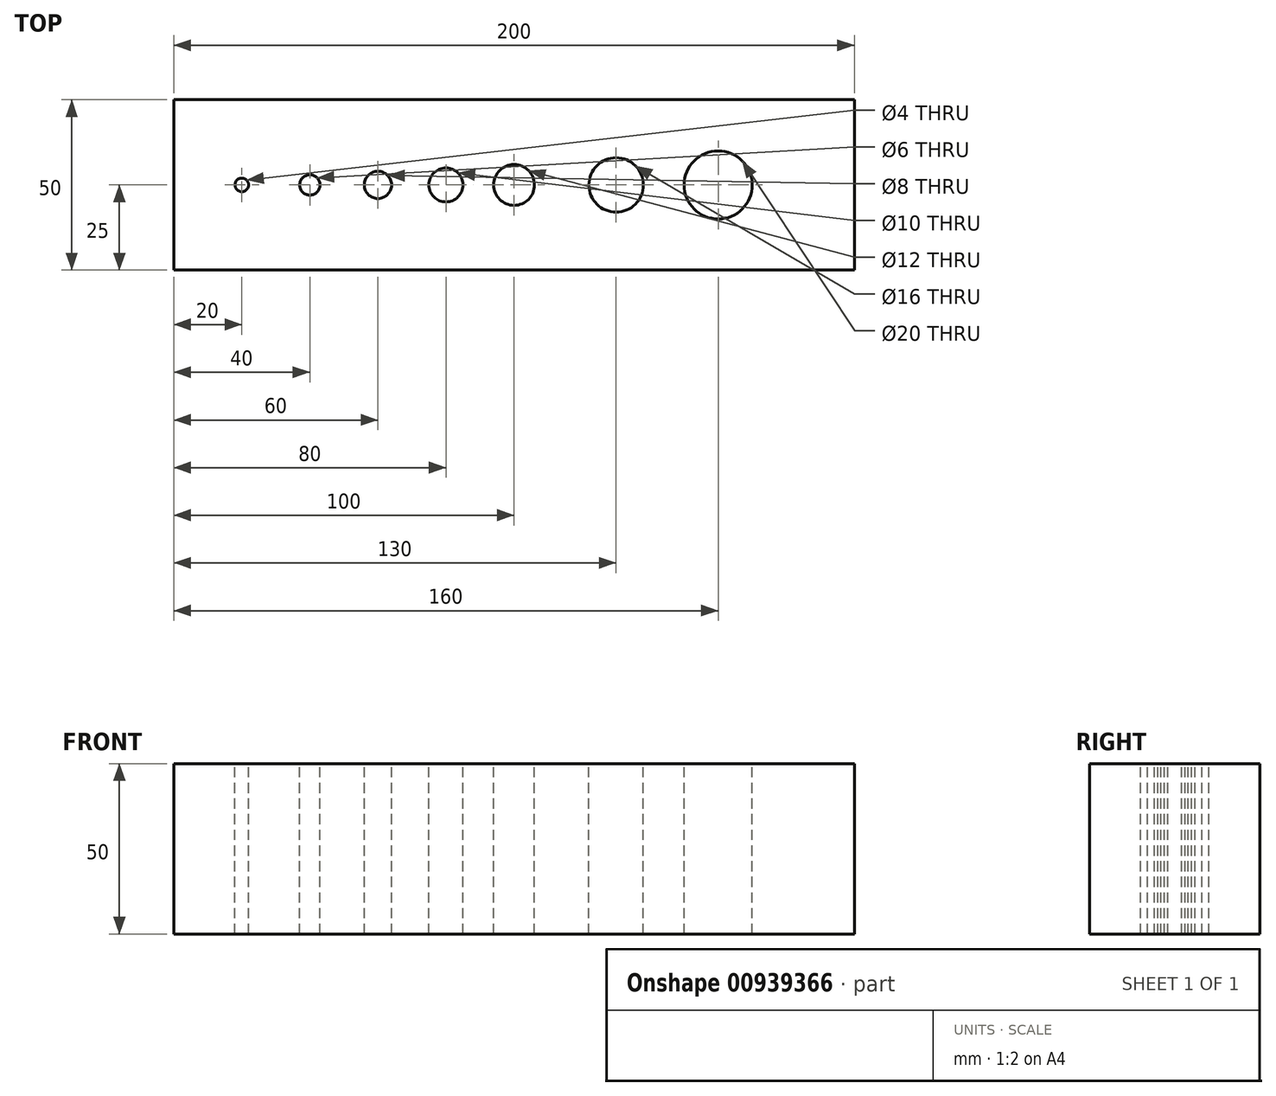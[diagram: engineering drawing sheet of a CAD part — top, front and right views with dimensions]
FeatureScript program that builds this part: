
annotation { "Feature Type Name" : "Feature", "Feature Type Description" : "" }
export const myFeature = defineFeature(function(context is Context, id is Id, definition is map)
    precondition{}
    {
        {
            var Q0;
            Q0=qCreatedBy(makeId("Top.planeOp"),FACE);
            var sketch = newSketch(context, id + "F0", { "sketchPlane" : qUnion([Q0])});
            skLineSegment(sketch, "E0.bottom", {"start": v(-100, 25) * mm, "end": v(100, 25) * mm});
            skLineSegment(sketch, "E0.top", {"start": v(-100, -25) * mm, "end": v(100, -25) * mm});
            skLineSegment(sketch, "E0.left", {"start": v(-100, 25) * mm, "end": v(-100, -25) * mm});
            skLineSegment(sketch, "E0.right", {"start": v(100, 25) * mm, "end": v(100, -25) * mm});
            skPoint(sketch, "E0.middle", {"position": v(0, 0) * mm});
            skSolve(sketch);
        }
        {
            var Q0;
            Q0=makeQuery(id+"F0.imprint","IMPRINT",FACE,{"disambiguationData":[TD([[makeQuery(id+"F0.imprint","IMPRINT",EDGE,{"derivedFrom":sQuery(id+"F0.wireOp",EDGE,"E0.bottom")}),-1.0]])]});
            extrude(context, id + "F1", {"entities" : qUnion([Q0]), "endBound" : BoundingType.SYMMETRIC, "depth" : 50 * mm, "offsetDistance" : 25.4 * mm});
        }
        {
            var Q0;
            Q0=makeQuery(id+"F1.opExtrude","CAP_FACE",FACE,{"disambiguationData":[OSD([sQuery(id+"F0.wireOp",EDGE,"E0.bottom"),sQuery(id+"F0.wireOp",EDGE,"E0.top"),sQuery(id+"F0.wireOp",EDGE,"E0.left"),sQuery(id+"F0.wireOp",EDGE,"E0.right")])],"isStart":false});
            var sketch = newSketch(context, id + "F2", { "sketchPlane" : qUnion([Q0])});
            skPoint(sketch, "E1", {"position": v(-80, 0) * mm});
            skPoint(sketch, "E2.1.0.0", {"position": v(-60, 0) * mm});
            skPoint(sketch, "E2.2.0.0", {"position": v(-40, 0) * mm});
            skPoint(sketch, "E2.3.0.0", {"position": v(-20, 0) * mm});
            skPoint(sketch, "E2.4.0.0", {"position": v(0, 0) * mm});
            skLineSegment(sketch, "E2.direction1", {"start": v(-80, 0) * mm, "end": v(-60, 0) * mm, "construction": true});
            skPoint(sketch, "E3.1.0.0", {"position": v(30, 0) * mm});
            skPoint(sketch, "E3.2.0.0", {"position": v(60, 0) * mm});
            skLineSegment(sketch, "E3.direction1", {"start": v(0, 0) * mm, "end": v(30, 0) * mm, "construction": true});
            skSolve(sketch);
        }
        {
            var Q0;
            Q0=sQuery(id+"F2.wireOp",VERTEX,"E2.direction1.start");
            var Q1;
            Q1=makeQuery(id+"F1.opExtrude","SWEPT_BODY",BODY,{"disambiguationData":[OSD([sQuery(id+"F0.wireOp",EDGE,"E0.bottom"),sQuery(id+"F0.wireOp",EDGE,"E0.top"),sQuery(id+"F0.wireOp",EDGE,"E0.left"),sQuery(id+"F0.wireOp",EDGE,"E0.right")])]});
            hole(context, id + "F3", {"style" : HoleStyle.SIMPLE, "endStyle" : HoleEndStyle.THROUGH, "standardTappedOrClearance" : lookupTablePath({ "standard" : "ISO", "size" : "4", "type" : "Drilled" }), "standardBlindInLast" : lookupTablePath({ "standard" : "ISO", "size" : "4", "type" : "Drilled" }), "holeDiameter" : 4 * mm, "majorDiameter" : 6.35 * mm, "tappedDepth" : 12.7 * mm, "tapClearance" : 3, "startFromSketch" : true, "locations" : qUnion([Q0]), "scope" : qUnion([Q1])});
        }
        {
            var Q0;
            Q0=sQuery(id+"F2.wireOp",VERTEX,"E2.direction1.end");
            var Q1;
            Q1=makeQuery(id+"F1.opExtrude","SWEPT_BODY",BODY,{"disambiguationData":[OSD([sQuery(id+"F0.wireOp",EDGE,"E0.bottom"),sQuery(id+"F0.wireOp",EDGE,"E0.top"),sQuery(id+"F0.wireOp",EDGE,"E0.left"),sQuery(id+"F0.wireOp",EDGE,"E0.right")])]});
            hole(context, id + "F4", {"style" : HoleStyle.SIMPLE, "endStyle" : HoleEndStyle.THROUGH, "standardTappedOrClearance" : lookupTablePath({ "standard" : "ISO", "size" : "6", "type" : "Drilled" }), "standardBlindInLast" : lookupTablePath({ "standard" : "ISO", "size" : "6", "type" : "Drilled" }), "holeDiameter" : 6 * mm, "majorDiameter" : 6.35 * mm, "tappedDepth" : 12.7 * mm, "tapClearance" : 3, "startFromSketch" : true, "locations" : qUnion([Q0]), "scope" : qUnion([Q1])});
        }
        {
            var Q0;
            Q0=sQuery(id+"F2.wireOp",VERTEX,"E2.2.0.0");
            var Q1;
            Q1=makeQuery(id+"F1.opExtrude","SWEPT_BODY",BODY,{"disambiguationData":[OSD([sQuery(id+"F0.wireOp",EDGE,"E0.bottom"),sQuery(id+"F0.wireOp",EDGE,"E0.top"),sQuery(id+"F0.wireOp",EDGE,"E0.left"),sQuery(id+"F0.wireOp",EDGE,"E0.right")])]});
            hole(context, id + "F5", {"style" : HoleStyle.SIMPLE, "endStyle" : HoleEndStyle.THROUGH, "standardTappedOrClearance" : lookupTablePath({ "standard" : "ISO", "size" : "8", "type" : "Drilled" }), "standardBlindInLast" : lookupTablePath({ "standard" : "ISO", "size" : "8", "type" : "Drilled" }), "holeDiameter" : 8 * mm, "majorDiameter" : 6.35 * mm, "tappedDepth" : 12.7 * mm, "tapClearance" : 3, "startFromSketch" : true, "locations" : qUnion([Q0]), "scope" : qUnion([Q1])});
        }
        {
            var Q0;
            Q0=sQuery(id+"F2.wireOp",VERTEX,"E2.3.0.0");
            var Q1;
            Q1=makeQuery(id+"F1.opExtrude","SWEPT_BODY",BODY,{"disambiguationData":[OSD([sQuery(id+"F0.wireOp",EDGE,"E0.bottom"),sQuery(id+"F0.wireOp",EDGE,"E0.top"),sQuery(id+"F0.wireOp",EDGE,"E0.left"),sQuery(id+"F0.wireOp",EDGE,"E0.right")])]});
            hole(context, id + "F6", {"style" : HoleStyle.SIMPLE, "endStyle" : HoleEndStyle.THROUGH, "standardTappedOrClearance" : lookupTablePath({ "standard" : "ISO", "size" : "10", "type" : "Drilled" }), "standardBlindInLast" : lookupTablePath({ "standard" : "ISO", "size" : "10", "type" : "Drilled" }), "holeDiameter" : 10 * mm, "majorDiameter" : 6.35 * mm, "tappedDepth" : 12.7 * mm, "tapClearance" : 3, "startFromSketch" : true, "locations" : qUnion([Q0]), "scope" : qUnion([Q1])});
        }
        {
            var Q0;
            Q0=sQuery(id+"F2.wireOp",VERTEX,"E2.4.0.0");
            var Q1;
            Q1=makeQuery(id+"F1.opExtrude","SWEPT_BODY",BODY,{"disambiguationData":[OSD([sQuery(id+"F0.wireOp",EDGE,"E0.bottom"),sQuery(id+"F0.wireOp",EDGE,"E0.top"),sQuery(id+"F0.wireOp",EDGE,"E0.left"),sQuery(id+"F0.wireOp",EDGE,"E0.right")])]});
            hole(context, id + "F7", {"style" : HoleStyle.SIMPLE, "endStyle" : HoleEndStyle.THROUGH, "standardTappedOrClearance" : lookupTablePath({ "standard" : "ISO", "size" : "12", "type" : "Drilled" }), "standardBlindInLast" : lookupTablePath({ "standard" : "ISO", "size" : "12", "type" : "Drilled" }), "holeDiameter" : 12 * mm, "majorDiameter" : 6.35 * mm, "tappedDepth" : 12.7 * mm, "tapClearance" : 3, "startFromSketch" : true, "locations" : qUnion([Q0]), "scope" : qUnion([Q1])});
        }
        {
            var Q0;
            Q0=sQuery(id+"F2.wireOp",VERTEX,"E3.1.0.0");
            var Q1;
            Q1=makeQuery(id+"F1.opExtrude","SWEPT_BODY",BODY,{"disambiguationData":[OSD([sQuery(id+"F0.wireOp",EDGE,"E0.bottom"),sQuery(id+"F0.wireOp",EDGE,"E0.top"),sQuery(id+"F0.wireOp",EDGE,"E0.left"),sQuery(id+"F0.wireOp",EDGE,"E0.right")])]});
            hole(context, id + "F8", {"style" : HoleStyle.SIMPLE, "endStyle" : HoleEndStyle.THROUGH, "standardTappedOrClearance" : lookupTablePath({ "standard" : "ISO", "size" : "16", "type" : "Drilled" }), "standardBlindInLast" : lookupTablePath({ "standard" : "ISO", "size" : "16", "type" : "Drilled" }), "holeDiameter" : 16 * mm, "majorDiameter" : 6.35 * mm, "tappedDepth" : 12.7 * mm, "tapClearance" : 3, "startFromSketch" : true, "locations" : qUnion([Q0]), "scope" : qUnion([Q1])});
        }
        {
            var Q0;
            Q0=sQuery(id+"F2.wireOp",VERTEX,"E3.2.0.0");
            var Q1;
            Q1=makeQuery(id+"F1.opExtrude","SWEPT_BODY",BODY,{"disambiguationData":[OSD([sQuery(id+"F0.wireOp",EDGE,"E0.bottom"),sQuery(id+"F0.wireOp",EDGE,"E0.top"),sQuery(id+"F0.wireOp",EDGE,"E0.left"),sQuery(id+"F0.wireOp",EDGE,"E0.right")])]});
            hole(context, id + "F9", {"style" : HoleStyle.SIMPLE, "endStyle" : HoleEndStyle.THROUGH, "standardTappedOrClearance" : lookupTablePath({ "standard" : "ISO", "size" : "20", "type" : "Drilled" }), "standardBlindInLast" : lookupTablePath({ "standard" : "ISO", "size" : "20", "type" : "Drilled" }), "holeDiameter" : 20 * mm, "majorDiameter" : 6.35 * mm, "tappedDepth" : 12.7 * mm, "tapClearance" : 3, "startFromSketch" : true, "locations" : qUnion([Q0]), "scope" : qUnion([Q1])});
        }
    });
